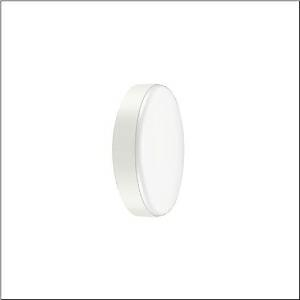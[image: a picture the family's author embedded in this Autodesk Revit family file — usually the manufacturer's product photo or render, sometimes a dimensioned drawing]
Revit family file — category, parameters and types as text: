
# Revit family: rondel_31_51wc10ma42a
name_source: partatom
category: Lighting Fixtures
units: mm (PartAtom-declared; Revit-internal decimal feet)

## family parameters
Cut with Voids When Loaded = No
Host = Face
Light Source = No
Part Type = Normal
Room Calculation Point = No
Round Connector Dimension = Use Diameter
Shared = No

## types (1)
- --- (1 x LED, 2550 lm, 19 W, 4000K)
    Apparent Load = 19 VA
    CIE Flux Codes = 44 75 94 94 100
    Color Rendering = 80
    Color Temperature = 4000K
    Default Elevation = 1800 mm
    Description = Rondel 31, wall and ceiling luminaire, primary optical cover: cover, of PC, opal, light emission: direct distribution, primary light characteristic: symmetric, installation type: surface-mounted, LED, rated luminous flux: 2.400lm, luminous efficacy: 125lm/W, light colour: 840, colour temperature: 4000K, with terminal, 3-pole, max. 2.5mm², mains connection: 220..240V, AC, 50/60Hz, rated input power: 19W, luminaire housing, of PC, traffic white (RAL 9016), diameter: 350mm, protection rating (complete): IP65, insulation class (complete): insulation class II (safety insulation), certification: CE, impact resistance: IK10, permissible storage temperature: -20..+60°C, packaging unit: 1 piece
    Height = 97 mm
    Lamp = 1 x LED
    Lamp Light Flux = 2550 lm
    Lamp Power = 19 W
    Lamp count = 1
    Length = 350 mm
    Luminous efficacy = 134 lm/W
    Manufacturer = Siteco
    ModVariant = No
    Model = 51WC10MA42A
    Mounting Place = Ceiling
    Mounting Type = Surface mounted
    Number of Poles = 1
    OnlyDefault = Yes
    Power Factor = 1
    Product Name = Rondel 31
    Product group = wall and ceiling luminaire
    ProductGroupID = 301
    Protection Class = Protection class II
    Protection Degree = IP 65
    RLX_Detail_Level = 1
    RlxData = <blob elided: 29989 chars, md5=ef33fa79>
    Socket = socket
    Standby Power = 0 W
    System Light Flux = 2550 lm
    System Power = 19 W
    Type Comments = factory setting: luminous flux: 100 % | (ON | ON)
    Type Image = l_1007027.jpg
    URL = http://relux.com
    VarID = @adj_060569
    Voltage = 0 V
    Weight = 0.00 kg
    Width = 0 mm  [stored 0 ft]

note: [stored X ft] marks values corroborated as IEEE doubles in the binary element streams (Revit-internal decimal feet)

## geometry (parser evidence)
native form markers: Blend x4, Sweep x15
no freeform markers — native parametric forms only
